FCSTD DOCUMENT  (FreeCAD 1.1R20260325 (Git shallow))
Label: Assembly
License: All rights reserved
LicenseURL: https://en.wikipedia.org/wiki/All_rights_reserved
objects: App::Link×6, App::Point×3, Assembly::JointGroup×3, Assembly::AssemblyObject×3, App::FeaturePython×1
EXTERNAL_REF file=Bracket001.FCStd obj=Body
EXTERNAL_REF file=Bracket001.FCStd obj=Body001
EXTERNAL_REF file=775DC.FCStd obj=Body
EXTERNAL_REF file=nema-17-stepper-motor/17HS4401S stepper motor.FCStd obj=Part
EXTERNAL_REF file=2gt-timing-pulley-2.snapshot.2/Timing Pulley 20 Teeth 2GT Bore 8mm for width 10mm.FCStd obj=Body001
EXTERNAL_REF file=20x20-aluminum-profile-v-slot-1.snapshot.12/20x20 aluminum profile V-slot.FCStd obj=Body

FEATURE [App::Point] Origin001
  Role = Origin
FEATURE [App::Point] Origin003
  Role = Origin
FEATURE [Assembly::JointGroup] Joints001
FEATURE [Assembly::AssemblyObject] Assembly001
  Group = -> [Joints001]
  Origin = -> Origin002
  Type = Assembly
FEATURE [App::Link] Body
  LinkedObject = -> <external Bracket001.FCStd>#Body
FEATURE [App::FeaturePython] GroundedJoint  # Assembly grounded joint (typed FeaturePython)
  ObjectToGround = -> Body
FEATURE [Assembly::JointGroup] Joints
  Group = -> [GroundedJoint]
FEATURE [App::Link] Body001
  LinkPlacement = pos=(0,-4.52995e-06,38) rot=(0,0,1;0rad)
  LinkedObject = -> <external Bracket001.FCStd>#Body001
  Placement = pos=(0,-4.52995e-06,38) rot=(0,0,1;0rad)
FEATURE [App::Link] Body002
  LinkPlacement = pos=(0.341489,0.341488,48.3415) rot=(0,0,1;0rad)
  LinkedObject = -> <external 775DC.FCStd>#Body
  Placement = pos=(0.341489,0.341488,48.3415) rot=(0,0,1;0rad)
FEATURE [App::Link] _17HS4401S_Stepper_Motor  label="17HS4401S Stepper Motor"
  LinkPlacement = pos=(0,4.17233e-06,-35) rot=(0,0,1;0rad)
  LinkedObject = -> <external nema-17-stepper-motor/17HS4401S stepper motor.FCStd>#Part
  Placement = pos=(0,4.17233e-06,-35) rot=(0,0,1;0rad)
FEATURE [App::Link] GT_2_20  label="GT-2-20"
  LinkPlacement = pos=(0,-1.43051e-05,120) rot=(0,0,1;0rad)
  LinkedObject = -> <external 2gt-timing-pulley-2.snapshot.2/Timing Pulley 20 Teeth 2GT Bore 8mm for width 10mm.FCStd>#Body001
  Placement = pos=(0,-1.43051e-05,120) rot=(0,0,1;0rad)
FEATURE [App::Point] Origin005  label="Origin006"
  Role = Origin
FEATURE [Assembly::JointGroup] Joints002
FEATURE [Assembly::AssemblyObject] Assembly002
  Group = -> [Joints002]
  Origin = -> Origin004
  Type = Assembly
FEATURE [App::Link] V_slot_base  label="V-slot base"
  LinkPlacement = pos=(40.612,0.311316,-125.559) rot=(0,0,1;0rad)
  LinkedObject = -> <external 20x20-aluminum-profile-v-slot-1.snapshot.12/20x20 aluminum profile V-slot.FCStd>#Body
  Placement = pos=(40.612,0.311316,-125.559) rot=(0,0,1;0rad)
FEATURE [Assembly::AssemblyObject] Assembly
  Group = -> [Joints,Assembly001,Body,GroundedJoint,Body001,Body002,_17HS4401S_Stepper_Motor,GT_2_20,Assembly002,V_slot_base]
  Origin = -> Origin
  Type = Assembly

RESOLVED EXTERNAL PARTS (link-assembly join: the EXTERNAL_REF files above that resolve inside this repo's crawl, each included once):
---- part 775DC.FCStd = doc fcstd_6108e077a56b ----
FCSTD DOCUMENT  (FreeCAD 1.1R20260325 (Git shallow))
Label: 775DC
License: All rights reserved
LicenseURL: https://en.wikipedia.org/wiki/All_rights_reserved
objects: Sketcher::SketchObject×5, PartDesign::Pad×5, PartDesign::Fillet×4, PartDesign::Body×1, App::Point×1
note: 38 computed .brp shape members not serialized (recipe doc carries the construction recipe); baked Part::Feature solids carry a one-line shape summary decoded from their .brp

FEATURE [Sketcher::SketchObject] Sketch
  ArcFitTolerance = 1e-06
  AttachmentSupport = -> [XY_Plane]
  ExternalTypes = [0]
  FullyConstrained = false
  MakeInternals = false
  MapMode = 5
  _ExternalGeoVersion = 0
  sketch-geometry (1):
    g0: Circle CenterX=-0.540205 CenterY=0 CenterZ=0 NormalX=0 NormalY=0 NormalZ=1 AngleXU=0 Radius=22.5
  constraints (2):
    c: Diameter(g0) = 45
    c: PointOnObject(g0,g-1)
FEATURE [PartDesign::Pad] Pad
  Direction = (0,0,1)
  Length = 66.5
  Length2 = 10
  Profile = -> Sketch
  ReferenceAxis = -> Sketch [N_Axis]
  Refine = true
  SideType = 0
  Suppressed = false
  Type = 0
  Type2 = 0
FEATURE [PartDesign::Fillet] Fillet
  Base = -> Pad [Edge3]
  BaseFeature = -> Pad
  Radius = 3
  Refine = true
  SupportTransform = false
  Suppressed = false
  UseAllEdges = false
FEATURE [Sketcher::SketchObject] Sketch001
  ArcFitTolerance = 1e-06
  AttachmentSupport = -> [Fillet]
  ExternalTypes = [0]
  FullyConstrained = true
  MakeInternals = false
  MapMode = 5
  Placement = pos=(0,0,66.5) rot=(0,0,1;0rad)
  _ExternalGeoVersion = 0
  sketch-geometry (1):
    g0: Circle CenterX=0 CenterY=0 CenterZ=0 NormalX=0 NormalY=0 NormalZ=1 AngleXU=0 Radius=8.75
  constraints (2):
    c: Diameter(g0) = 17.5
    c: Coincident(g0,g-1)
FEATURE [PartDesign::Pad] Pad001
  BaseFeature = -> Fillet
  Direction = (0,0,1)
  Length = 2
  Length2 = 10
  Profile = -> Sketch001
  ReferenceAxis = -> Sketch001 [N_Axis]
  Refine = true
  SideType = 0
  Suppressed = false
  Type = 0
  Type2 = 0
FEATURE [PartDesign::Fillet] Fillet001
  Base = -> Pad001 [Edge8]
  BaseFeature = -> Pad001
  Radius = 1
  Refine = true
  SupportTransform = false
  Suppressed = false
  UseAllEdges = false
FEATURE [Sketcher::SketchObject] Sketch002
  ArcFitTolerance = 1e-06
  AttachmentSupport = -> [Fillet001]
  ExternalTypes = [0]
  FullyConstrained = true
  MakeInternals = false
  MapMode = 5
  Placement = pos=(0,0,68.5) rot=(0,0,1;0rad)
  _ExternalGeoVersion = 0
  sketch-geometry (1):
    g0: Circle CenterX=0 CenterY=0 CenterZ=0 NormalX=0 NormalY=0 NormalZ=1 AngleXU=0 Radius=2.5
  constraints (2):
    c: Diameter(g0) = 5
    c: Coincident(g0,g-1)
FEATURE [PartDesign::Pad] Pad002
  BaseFeature = -> Fillet001
  Direction = (0,0,1)
  Length = 16
  Length2 = 10
  Profile = -> Sketch002
  ReferenceAxis = -> Sketch002 [N_Axis]
  Refine = true
  SideType = 0
  Suppressed = false
  Type = 0
  Type2 = 0
FEATURE [PartDesign::Fillet] Fillet002
  Base = -> Pad002 [Edge11]
  BaseFeature = -> Pad002
  Radius = 1
  Refine = true
  SupportTransform = false
  Suppressed = false
  UseAllEdges = false
FEATURE [Sketcher::SketchObject] Sketch003
  ArcFitTolerance = 1e-06
  AttachmentSupport = -> [Fillet002]
  ExternalTypes = [0]
  FullyConstrained = true
  MakeInternals = false
  MapMode = 5
  Placement = pos=(0,0,0) rot=(1,0,0;3.14159rad)
  _ExternalGeoVersion = 0
  sketch-geometry (1):
    g0: Circle CenterX=0 CenterY=0 CenterZ=0 NormalX=0 NormalY=0 NormalZ=1 AngleXU=0 Radius=8.75
  constraints (2):
    c: Diameter(g0) = 17.5
    c: Coincident(g0,g-1)
FEATURE [PartDesign::Pad] Pad003
  BaseFeature = -> Fillet002
  Direction = (0,0,-1)
  Length = 2
  Length2 = 10
  Profile = -> Sketch003
  ReferenceAxis = -> Sketch003 [N_Axis]
  Refine = true
  SideType = 0
  Suppressed = false
  Type = 0
  Type2 = 0
FEATURE [PartDesign::Fillet] Fillet003
  Base = -> Pad003 [Edge18]
  BaseFeature = -> Pad003
  Radius = 1
  Refine = true
  SupportTransform = false
  Suppressed = false
  UseAllEdges = false
FEATURE [Sketcher::SketchObject] Sketch004
  ArcFitTolerance = 1e-06
  AttachmentSupport = -> [Fillet003]
  ExternalTypes = [0]
  FullyConstrained = true
  MakeInternals = false
  MapMode = 5
  Placement = pos=(0,0,-2) rot=(1,0,0;3.14159rad)
  _ExternalGeoVersion = 0
  sketch-geometry (1):
    g0: Circle CenterX=0 CenterY=0 CenterZ=0 NormalX=0 NormalY=0 NormalZ=1 AngleXU=0 Radius=2.5
  constraints (2):
    c: Diameter(g0) = 5
    c: Coincident(g0,g-1)
FEATURE [PartDesign::Pad] Pad004
  BaseFeature = -> Fillet003
  Direction = (0,0,-1)
  Length = 20
  Length2 = 10
  Profile = -> Sketch004
  ReferenceAxis = -> Sketch004 [N_Axis]
  Refine = true
  SideType = 0
  Suppressed = false
  Type = 0
  Type2 = 0
FEATURE [PartDesign::Body] Body
  AllowCompound = false
  Group = -> [Sketch,Pad,Fillet,Sketch001,Pad001,Fillet001,Sketch002,Pad002,Fillet002,Sketch003,Pad003,Fillet003,Sketch004,Pad004]
  Origin = -> Origin
  Tip = -> Pad004
FEATURE [App::Point] Origin001  label="Origin"
  Role = Origin
---- part Bracket001.FCStd = doc fcstd_f8667adaf7e8 ----
FCSTD DOCUMENT  (FreeCAD 1.1R20260325 (Git shallow))
Label: Bracket001
License: All rights reserved
LicenseURL: https://en.wikipedia.org/wiki/All_rights_reserved
objects: Sketcher::SketchObject×18, PartDesign::Pocket×9, PartDesign::Pad×7, PartDesign::Chamfer×3, PartDesign::Body×2, App::Point×2
note: 95 computed .brp shape members not serialized (recipe doc carries the construction recipe); baked Part::Feature solids carry a one-line shape summary decoded from their .brp

FEATURE [Sketcher::SketchObject] Sketch
  ArcFitTolerance = 1e-06
  AttachmentSupport = -> [XY_Plane]
  ExternalTypes = [0]
  FullyConstrained = true
  MakeInternals = false
  MapMode = 5
  _ExternalGeoVersion = 0
  sketch-geometry (5):
    g0: LineSegment StartX=-31 StartY=-31 StartZ=0 EndX=31 EndY=-31 EndZ=0
    g1: LineSegment StartX=31 StartY=-31 StartZ=0 EndX=31 EndY=31 EndZ=0
    g2: LineSegment StartX=31 StartY=31 StartZ=0 EndX=-31 EndY=31 EndZ=0
    g3: LineSegment StartX=-31 StartY=31 StartZ=0 EndX=-31 EndY=-31 EndZ=0
    g4: GeomPoint [constr] X=0 Y=0 Z=0
  constraints (12):
    c: Coincident(g0,g1)
    c: Coincident(g1,g2)
    c: Coincident(g2,g3)
    c: Coincident(g3,g0)
    c: Horizontal(g0)
    c: Horizontal(g2)
    c: Vertical(g1)
    c: Vertical(g3)
    c: Symmetric(g2,g0,g4)
    c: Distance(g1,g3) = 62
    c: Distance(g0,g2) = 62
    c: Coincident(g4,g-1)
FEATURE [PartDesign::Pad] Pad
  Direction = (0,0,1)
  Length = 8
  Length2 = 10
  Profile = -> Sketch
  ReferenceAxis = -> Sketch [N_Axis]
  Refine = true
  SideType = 0
  Suppressed = false
  Type = 0
  Type2 = 0
FEATURE [Sketcher::SketchObject] Sketch001
  ArcFitTolerance = 1e-06
  AttachmentSupport = -> [Pad]
  ExternalGeometry = -> [Pad]
  ExternalTypes = [0]
  FullyConstrained = true
  MakeInternals = false
  MapMode = 5
  Placement = pos=(0,0,8) rot=(0,0,1;0rad)
  _ExternalGeoVersion = 0
  sketch-geometry (4):
    g0: LineSegment StartX=-31 StartY=31 StartZ=0 EndX=-31 EndY=21 EndZ=0
    g1: LineSegment StartX=-31 StartY=21 StartZ=0 EndX=31 EndY=21 EndZ=0
    g2: LineSegment StartX=31 StartY=21 StartZ=0 EndX=31 EndY=31 EndZ=0
    g3: LineSegment StartX=31 StartY=31 StartZ=0 EndX=-31 EndY=31 EndZ=0
  constraints (11):
    c: Coincident(g0,g1)
    c: Coincident(g1,g2)
    c: Coincident(g2,g3)
    c: Coincident(g3,g0)
    c: Vertical(g0)
    c: Vertical(g2)
    c: Horizontal(g1)
    c: Horizontal(g3)
    c: Distance(g0,g2) = 62
    c: Distance(g1,g3) = 10
    c: Coincident(g0,g-3)
FEATURE [PartDesign::Pad] Pad001
  BaseFeature = -> Pad
  Direction = (0,0,1)
  Length = 30
  Length2 = 10
  Profile = -> Sketch001
  ReferenceAxis = -> Sketch001 [N_Axis]
  Refine = true
  SideType = 0
  Suppressed = false
  Type = 0
  Type2 = 0
FEATURE [Sketcher::SketchObject] Sketch002
  ArcFitTolerance = 1e-06
  AttachmentSupport = -> [Pad001]
  ExternalGeometry = -> [Pad001]
  ExternalTypes = [0]
  FullyConstrained = true
  MakeInternals = false
  MapMode = 5
  Placement = pos=(0,0,8) rot=(0,0,1;0rad)
  _ExternalGeoVersion = 0
  sketch-geometry (4):
    g0: LineSegment StartX=-31 StartY=-31 StartZ=0 EndX=31 EndY=-31 EndZ=0
    g1: LineSegment StartX=31 StartY=-31 StartZ=0 EndX=31 EndY=-21 EndZ=0
    g2: LineSegment StartX=31 StartY=-21 StartZ=0 EndX=-31 EndY=-21 EndZ=0
    g3: LineSegment StartX=-31 StartY=-21 StartZ=0 EndX=-31 EndY=-31 EndZ=0
  constraints (11):
    c: Coincident(g0,g1)
    c: Coincident(g1,g2)
    c: Coincident(g2,g3)
    c: Coincident(g3,g0)
    c: Horizontal(g0)
    c: Horizontal(g2)
    c: Vertical(g1)
    c: Vertical(g3)
    c: Distance(g1,g3) = 62
    c: Distance(g0,g2) = 10
    c: Coincident(g0,g-3)
FEATURE [PartDesign::Pad] Pad002
  BaseFeature = -> Pad001
  Direction = (0,0,1)
  Length = 30
  Length2 = 10
  Profile = -> Sketch002
  ReferenceAxis = -> Sketch002 [N_Axis]
  Refine = true
  SideType = 0
  Suppressed = false
  Type = 0
  Type2 = 0
FEATURE [Sketcher::SketchObject] Sketch003
  ArcFitTolerance = 1e-06
  AttachmentSupport = -> [Pad002]
  ExternalGeometry = -> [Pad002]
  ExternalTypes = [0]
  FullyConstrained = true
  MakeInternals = false
  MapMode = 5
  Placement = pos=(0,0,8) rot=(0,0,1;0rad)
  _ExternalGeoVersion = 0
  sketch-geometry (11):
    g0: LineSegment [constr] StartX=-31 StartY=21 StartZ=0 EndX=-31 EndY=-21 EndZ=0
    g1: LineSegment [constr] StartX=31 StartY=21 StartZ=0 EndX=31 EndY=-21 EndZ=0
    g2: LineSegment [constr] StartX=-15.5 StartY=-15.5 StartZ=0 EndX=15.5 EndY=-15.5 EndZ=0
    g3: LineSegment [constr] StartX=15.5 StartY=-15.5 StartZ=0 EndX=15.5 EndY=15.5 EndZ=0
    g4: LineSegment [constr] StartX=15.5 StartY=15.5 StartZ=0 EndX=-15.5 EndY=15.5 EndZ=0
    g5: LineSegment [constr] StartX=-15.5 StartY=15.5 StartZ=0 EndX=-15.5 EndY=-15.5 EndZ=0
    g6: GeomPoint [constr] X=0 Y=0 Z=0
    g7: Circle CenterX=-15.5 CenterY=15.5 CenterZ=0 NormalX=0 NormalY=0 NormalZ=1 AngleXU=0 Radius=1.6
    g8: Circle CenterX=15.5 CenterY=15.5 CenterZ=0 NormalX=0 NormalY=0 NormalZ=1 AngleXU=0 Radius=1.6
    g9: Circle CenterX=-15.5 CenterY=-15.5 CenterZ=0 NormalX=0 NormalY=0 NormalZ=1 AngleXU=0 Radius=1.6
    g10: Circle CenterX=15.5 CenterY=-15.5 CenterZ=0 NormalX=0 NormalY=0 NormalZ=1 AngleXU=0 Radius=1.6
  constraints (24):
    c: Coincident(g0,g-3)
    c: Coincident(g0,g-4)
    c: Coincident(g1,g-3)
    c: Coincident(g1,g-4)
    c: Coincident(g2,g3)
    c: Coincident(g3,g4)
    c: Coincident(g4,g5)
    c: Coincident(g5,g2)
    c: Horizontal(g2)
    c: Horizontal(g4)
    c: Vertical(g3)
    c: Vertical(g5)
    c: Symmetric(g4,g2,g6)
    c: Distance(g3,g5) = 31
    c: Distance(g2,g4) = 31
    c: Coincident(g6,g-1)
    c: Diameter(g7) = 3.2
    c: Coincident(g7,g4)
    c: Diameter(g8) = 3.2
    c: Coincident(g8,g3)
    c: Diameter(g9) = 3.2
    c: Coincident(g9,g2)
    c: Diameter(g10) = 3.2
    c: Coincident(g10,g2)
FEATURE [PartDesign::Pocket] Pocket
  BaseFeature = -> Pad002
  Direction = (0,0,-1)
  Length = 5
  Length2 = 5
  Profile = -> Sketch003
  ReferenceAxis = -> Sketch003 [N_Axis]
  Refine = true
  SideType = 0
  Suppressed = false
  Type = 1
  Type2 = 0
FEATURE [PartDesign::Chamfer] Chamfer
  Angle = 45
  Base = -> Pocket [Edge31,Edge29,Edge25,Edge27]
  BaseFeature = -> Pocket
  ChamferType = 0
  FlipDirection = false
  Refine = true
  Size = 2
  Size2 = 1
  SupportTransform = false
  Suppressed = false
  UseAllEdges = false
FEATURE [Sketcher::SketchObject] Sketch004
  ArcFitTolerance = 1e-06
  AttachmentSupport = -> [Chamfer]
  ExternalGeometry = -> [Chamfer]
  ExternalTypes = [0]
  FullyConstrained = true
  MakeInternals = false
  MapMode = 5
  Placement = pos=(0,0,38) rot=(0,0,1;0rad)
  _ExternalGeoVersion = 0
  sketch-geometry (5):
    g0: LineSegment [constr] StartX=-21 StartY=31 StartZ=0 EndX=-21 EndY=21 EndZ=0
    g1: LineSegment [constr] StartX=21 StartY=31 StartZ=0 EndX=21 EndY=21 EndZ=0
    g2: LineSegment [constr] StartX=-31 StartY=26 StartZ=0 EndX=31 EndY=26 EndZ=0
    g3: Circle CenterX=-21 CenterY=26 CenterZ=0 NormalX=0 NormalY=0 NormalZ=1 AngleXU=0 Radius=1.75
    g4: Circle CenterX=21 CenterY=26 CenterZ=0 NormalX=0 NormalY=0 NormalZ=1 AngleXU=0 Radius=1.75
  constraints (14):
    c: PointOnObject(g0,g-3)
    c: PointOnObject(g0,g-4)
    c: Vertical(g0)
    c: PointOnObject(g1,g-3)
    c: PointOnObject(g1,g-4)
    c: Vertical(g1)
    c: Distance(g-5,g0) = 10
    c: Distance(g-6,g1) = 10
    c: Symmetric(g-5,g-5,g2)
    c: Symmetric(g-6,g-6,g2)
    c: Diameter(g3) = 3.5
    c: Symmetric(g0,g0,g3)
    c: Diameter(g4) = 3.5
    c: Symmetric(g1,g1,g4)
FEATURE [PartDesign::Pocket] Pocket001
  BaseFeature = -> Chamfer
  Direction = (0,0,-1)
  Length = 12
  Length2 = 5
  Profile = -> Sketch004
  ReferenceAxis = -> Sketch004 [N_Axis]
  Refine = true
  SideType = 0
  Suppressed = false
  Type = 0
  Type2 = 0
FEATURE [Sketcher::SketchObject] Sketch005
  ArcFitTolerance = 1e-06
  AttachmentSupport = -> [Pocket001]
  ExternalGeometry = -> [Pocket001]
  ExternalTypes = [0]
  FullyConstrained = true
  MakeInternals = false
  MapMode = 5
  Placement = pos=(0,0,38) rot=(0,0,1;0rad)
  _ExternalGeoVersion = 0
  sketch-geometry (5):
    g0: LineSegment [constr] StartX=-31 StartY=-26 StartZ=0 EndX=31 EndY=-26 EndZ=0
    g1: LineSegment [constr] StartX=-21 StartY=26 StartZ=0 EndX=-21 EndY=-26 EndZ=0
    g2: LineSegment [constr] StartX=21 StartY=26 StartZ=0 EndX=21 EndY=-26 EndZ=0
    g3: Circle CenterX=-21 CenterY=-26 CenterZ=0 NormalX=0 NormalY=0 NormalZ=1 AngleXU=0 Radius=1.75
    g4: Circle CenterX=21 CenterY=-26 CenterZ=0 NormalX=0 NormalY=0 NormalZ=1 AngleXU=0 Radius=1.75
  constraints (12):
    c: Symmetric(g-5,g-5,g0)
    c: Symmetric(g-6,g-6,g0)
    c: Coincident(g1,g-3)
    c: PointOnObject(g1,g0)
    c: Vertical(g1)
    c: Coincident(g2,g-4)
    c: PointOnObject(g2,g0)
    c: Vertical(g2)
    c: Diameter(g3) = 3.5
    c: Coincident(g3,g1)
    c: Diameter(g4) = 3.5
    c: Coincident(g4,g2)
FEATURE [PartDesign::Pocket] Pocket002
  BaseFeature = -> Pocket001
  Direction = (0,0,-1)
  Length = 12
  Length2 = 5
  Profile = -> Sketch005
  ReferenceAxis = -> Sketch005 [N_Axis]
  Refine = true
  SideType = 0
  Suppressed = false
  Type = 0
  Type2 = 0
FEATURE [Sketcher::SketchObject] Sketch006
  ArcFitTolerance = 1e-06
  AttachmentSupport = -> [Pocket002]
  ExternalTypes = [0]
  FullyConstrained = true
  MakeInternals = false
  MapMode = 5
  Placement = pos=(0,0,8) rot=(0,0,1;0rad)
  _ExternalGeoVersion = 0
  sketch-geometry (1):
    g0: Circle CenterX=0 CenterY=0 CenterZ=0 NormalX=0 NormalY=0 NormalZ=1 AngleXU=0 Radius=12
  constraints (2):
    c: Diameter(g0) = 24
    c: Coincident(g0,g-1)
FEATURE [PartDesign::Pocket] Pocket003
  BaseFeature = -> Pocket002
  Direction = (0,0,-1)
  Length = 5
  Length2 = 5
  Profile = -> Sketch006
  ReferenceAxis = -> Sketch006 [N_Axis]
  Refine = true
  SideType = 0
  Suppressed = false
  Type = 1
  Type2 = 0
FEATURE [Sketcher::SketchObject] Sketch007
  ArcFitTolerance = 1e-06
  AttachmentSupport = -> [XY_Plane001]
  ExternalTypes = [0]
  FullyConstrained = true
  MakeInternals = false
  MapMode = 5
  _ExternalGeoVersion = 0
  sketch-geometry (5):
    g0: LineSegment StartX=-31 StartY=-31 StartZ=0 EndX=31 EndY=-31 EndZ=0
    g1: LineSegment StartX=31 StartY=-31 StartZ=0 EndX=31 EndY=31 EndZ=0
    g2: LineSegment StartX=31 StartY=31 StartZ=0 EndX=-31 EndY=31 EndZ=0
    g3: LineSegment StartX=-31 StartY=31 StartZ=0 EndX=-31 EndY=-31 EndZ=0
    g4: GeomPoint [constr] X=0 Y=0 Z=0
  constraints (12):
    c: Coincident(g0,g1)
    c: Coincident(g1,g2)
    c: Coincident(g2,g3)
    c: Coincident(g3,g0)
    c: Horizontal(g0)
    c: Horizontal(g2)
    c: Vertical(g1)
    c: Vertical(g3)
    c: Symmetric(g2,g0,g4)
    c: Distance(g1,g3) = 62
    c: Distance(g0,g2) = 62
    c: Coincident(g4,g-1)
FEATURE [PartDesign::Pad] Pad003
  Direction = (0,0,1)
  Length = 8
  Length2 = 10
  Profile = -> Sketch007
  ReferenceAxis = -> Sketch007 [N_Axis]
  Refine = true
  SideType = 0
  Suppressed = false
  Type = 0
  Type2 = 0
FEATURE [Sketcher::SketchObject] Sketch008
  ArcFitTolerance = 1e-06
  AttachmentSupport = -> [Pad003]
  ExternalGeometry = -> [Pad003]
  ExternalTypes = [0]
  FullyConstrained = false
  MakeInternals = false
  MapMode = 5
  Placement = pos=(0,0,8) rot=(0,0,1;0rad)
  _ExternalGeoVersion = 0
  sketch-geometry (18):
    g0: LineSegment [constr] StartX=-31 StartY=31 StartZ=0 EndX=-31 EndY=21 EndZ=0
    g1: LineSegment [constr] StartX=-31 StartY=21 StartZ=0 EndX=31 EndY=21 EndZ=0
    g2: LineSegment [constr] StartX=31 StartY=21 StartZ=0 EndX=31 EndY=31 EndZ=0
    g3: LineSegment [constr] StartX=31 StartY=31 StartZ=0 EndX=-31 EndY=31 EndZ=0
    g4: LineSegment [constr] StartX=31 StartY=-31 StartZ=0 EndX=31 EndY=-21 EndZ=0
    g5: LineSegment [constr] StartX=31 StartY=-21 StartZ=0 EndX=-31 EndY=-21 EndZ=0
    g6: LineSegment [constr] StartX=-31 StartY=-21 StartZ=0 EndX=-31 EndY=-31 EndZ=0
    g7: LineSegment [constr] StartX=-31 StartY=-31 StartZ=0 EndX=31 EndY=-31 EndZ=0
    g8: LineSegment [constr] StartX=-31 StartY=-26 StartZ=0 EndX=31 EndY=-26 EndZ=0
    g9: LineSegment [constr] StartX=-31 StartY=26 StartZ=0 EndX=31 EndY=26 EndZ=0
    g10: LineSegment [constr] StartX=-21 StartY=31 StartZ=0 EndX=-21 EndY=21 EndZ=0
    g11: LineSegment [constr] StartX=-21 StartY=21 StartZ=0 EndX=-21 EndY=-26 EndZ=0
    g12: LineSegment [constr] StartX=21 StartY=31 StartZ=0 EndX=21 EndY=21 EndZ=0
    g13: LineSegment [constr] StartX=21 StartY=21 StartZ=0 EndX=21 EndY=-26 EndZ=0
    g14: Circle CenterX=-21 CenterY=26 CenterZ=0 NormalX=0 NormalY=0 NormalZ=1 AngleXU=0 Radius=1.65
    g15: Circle CenterX=21 CenterY=26 CenterZ=0 NormalX=0 NormalY=0 NormalZ=1 AngleXU=0 Radius=1.65
    g16: Circle CenterX=-21 CenterY=-26 CenterZ=0 NormalX=0 NormalY=0 NormalZ=1 AngleXU=0 Radius=1.65
    g17: Circle CenterX=20.8764 CenterY=-26 CenterZ=0 NormalX=0 NormalY=0 NormalZ=1 AngleXU=0 Radius=1.65
  constraints (48):
    c: Coincident(g0,g1)
    c: Coincident(g1,g2)
    c: Coincident(g2,g3)
    c: Coincident(g3,g0)
    c: Vertical(g0)
    c: Vertical(g2)
    c: Horizontal(g1)
    c: Horizontal(g3)
    c: Distance(g0,g2) = 62
    c: Distance(g1,g3) = 10
    c: Coincident(g0,g-3)
    c: Coincident(g4,g5)
    c: Coincident(g5,g6)
    c: Coincident(g6,g7)
    c: Coincident(g7,g4)
    c: Vertical(g4)
    c: Vertical(g6)
    c: Horizontal(g5)
    c: Horizontal(g7)
    c: Distance(g4,g6) = 62
    c: Distance(g5,g7) = 10
    c: Coincident(g4,g-4)
    c: Symmetric(g6,g6,g8)
    c: Symmetric(g4,g4,g8)
    c: Symmetric(g0,g0,g9)
    c: Symmetric(g2,g2,g9)
    c: PointOnObject(g10,g3)
    c: PointOnObject(g10,g1)
    c: Vertical(g10)
    c: Distance(g0,g10) = 10
    c: Coincident(g11,g10)
    c: PointOnObject(g11,g8)
    c: Vertical(g11)
    c: PointOnObject(g12,g3)
    c: PointOnObject(g12,g1)
    c: Vertical(g12)
    c: Distance(g2,g12) = 10
    c: Coincident(g13,g12)
    c: PointOnObject(g13,g8)
    c: Vertical(g13)
    c: Diameter(g14) = 3.3
    c: Symmetric(g10,g10,g14)
    c: Diameter(g15) = 3.3
    c: Symmetric(g12,g12,g15)
    c: Diameter(g16) = 3.3
    c: Coincident(g16,g11)
    c: Diameter(g17) = 3.3
    c: PointOnObject(g17,g8)
FEATURE [PartDesign::Pocket] Pocket004
  BaseFeature = -> Pad003
  Direction = (0,0,-1)
  Length = 5
  Length2 = 5
  Profile = -> Sketch008
  ReferenceAxis = -> Sketch008 [N_Axis]
  Refine = true
  SideType = 0
  Suppressed = false
  Type = 1
  Type2 = 0
FEATURE [PartDesign::Chamfer] Chamfer001
  Angle = 45
  Base = -> Pocket004 [Edge18,Edge20,Edge19,Edge17]
  BaseFeature = -> Pocket004
  ChamferType = 0
  FlipDirection = false
  Refine = true
  Size = 2
  Size2 = 1
  SupportTransform = false
  Suppressed = false
  UseAllEdges = false
FEATURE [Sketcher::SketchObject] Sketch009
  ArcFitTolerance = 1e-06
  AttachmentSupport = -> [Chamfer001]
  ExternalTypes = [0]
  FullyConstrained = true
  MakeInternals = false
  MapMode = 5
  Placement = pos=(0,0,8) rot=(0,0,1;0rad)
  _ExternalGeoVersion = 0
  sketch-geometry (2):
    g0: Circle CenterX=0 CenterY=0 CenterZ=0 NormalX=0 NormalY=0 NormalZ=1 AngleXU=0 Radius=21.25
    g1: Circle CenterX=0 CenterY=0 CenterZ=0 NormalX=0 NormalY=0 NormalZ=1 AngleXU=0 Radius=27.75
  constraints (4):
    c: Diameter(g0) = 42.5
    c: Coincident(g0,g-1)
    c: Diameter(g1) = 55.5
    c: Coincident(g1,g0)
FEATURE [PartDesign::Pad] Pad004
  BaseFeature = -> Chamfer001
  Direction = (0,0,1)
  Length = 34
  Length2 = 10
  Profile = -> Sketch009
  ReferenceAxis = -> Sketch009 [N_Axis]
  Refine = true
  SideType = 0
  Suppressed = false
  Type = 0
  Type2 = 0
FEATURE [Sketcher::SketchObject] Sketch010
  ArcFitTolerance = 1e-06
  AttachmentSupport = -> [Pad004]
  ExternalTypes = [0]
  FullyConstrained = true
  MakeInternals = false
  MapMode = 5
  Placement = pos=(0,0,8) rot=(0,0,1;0rad)
  _ExternalGeoVersion = 0
  sketch-geometry (1):
    g0: Circle CenterX=0 CenterY=0 CenterZ=0 NormalX=0 NormalY=0 NormalZ=1 AngleXU=0 Radius=12
  constraints (2):
    c: Diameter(g0) = 24
    c: Coincident(g0,g-1)
FEATURE [PartDesign::Pocket] Pocket005
  BaseFeature = -> Pad004
  Direction = (0,0,-1)
  Length = 5
  Length2 = 5
  Profile = -> Sketch010
  ReferenceAxis = -> Sketch010 [N_Axis]
  Refine = true
  SideType = 0
  Suppressed = false
  Type = 1
  Type2 = 0
FEATURE [Sketcher::SketchObject] Sketch011
  ArcFitTolerance = 1e-06
  AttachmentSupport = -> [Pocket005]
  ExternalTypes = [0]
  FullyConstrained = false
  MakeInternals = false
  MapMode = 5
  Placement = pos=(0,0,42) rot=(0,0,1;0rad)
  _ExternalGeoVersion = 0
  sketch-geometry (5):
    g0: LineSegment StartX=-2.38976 StartY=32.2002 StartZ=0 EndX=-2.38976 EndY=16.9452 EndZ=0
    g1: LineSegment StartX=-2.38976 StartY=16.9452 StartZ=0 EndX=2.38975 EndY=16.9452 EndZ=0
    g2: LineSegment StartX=2.38975 StartY=16.9452 StartZ=0 EndX=2.38975 EndY=32.2002 EndZ=0
    g3: LineSegment StartX=2.38975 StartY=32.2002 StartZ=0 EndX=-2.38976 EndY=32.2002 EndZ=0
    g4: GeomPoint [constr] X=0 Y=24.5727 Z=0
  constraints (10):
    c: Coincident(g0,g1)
    c: Coincident(g1,g2)
    c: Coincident(g2,g3)
    c: Coincident(g3,g0)
    c: Vertical(g0)
    c: Vertical(g2)
    c: Horizontal(g1)
    c: Horizontal(g3)
    c: Symmetric(g2,g0,g4)
    c: PointOnObject(g4,g-2)
FEATURE [PartDesign::Pocket] Pocket006
  BaseFeature = -> Pocket005
  Direction = (0,0,-1)
  Length = 34
  Length2 = 5
  Profile = -> Sketch011
  ReferenceAxis = -> Sketch011 [N_Axis]
  Refine = true
  SideType = 0
  Suppressed = false
  Type = 0
  Type2 = 0
FEATURE [Sketcher::SketchObject] Sketch012
  ArcFitTolerance = 1e-06
  AttachmentSupport = -> [Pocket006]
  ExternalTypes = [0]
  FullyConstrained = false
  MakeInternals = false
  MapMode = 5
  Placement = pos=(0,0,8) rot=(0,0,1;0rad)
  _ExternalGeoVersion = 0
  sketch-geometry (2):
    g0: Circle CenterX=-18.7387 CenterY=0 CenterZ=0 NormalX=0 NormalY=0 NormalZ=1 AngleXU=0 Radius=2.4
    g1: Circle CenterX=18.7387 CenterY=0 CenterZ=0 NormalX=0 NormalY=0 NormalZ=1 AngleXU=0 Radius=2.4
  constraints (3):
    c: Diameter(g0) = 4.8
    c: PointOnObject(g0,g-1)
    c: Diameter(g1) = 4.8
FEATURE [PartDesign::Pocket] Pocket007
  BaseFeature = -> Pocket006
  Direction = (0,0,-1)
  Length = 5
  Length2 = 5
  Profile = -> Sketch012
  ReferenceAxis = -> Sketch012 [N_Axis]
  Refine = true
  SideType = 0
  Suppressed = false
  Type = 1
  Type2 = 0
FEATURE [Sketcher::SketchObject] Sketch013
  ArcFitTolerance = 1e-06
  AttachmentSupport = -> [Pocket007]
  ExternalTypes = [0]
  FullyConstrained = true
  MakeInternals = false
  MapMode = 5
  Placement = pos=(0,0,8) rot=(0,0,1;0rad)
  _ExternalGeoVersion = 0
FEATURE [PartDesign::Body] Body001
  AllowCompound = false
  Group = -> [Sketch007,Pad003,Sketch008,Pocket004,Chamfer001,Sketch009,Pad004,Sketch010,Pocket005,Sketch011,Pocket006,Sketch012,Pocket007,Sketch013]
  Origin = -> Origin001
  Placement = pos=(0,0,38) rot=(0,0,1;0rad)
  Tip = -> Pocket007
FEATURE [App::Point] Origin002  label="Origin"
  Role = Origin
FEATURE [App::Point] Origin003  label="Origin"
  Role = Origin
FEATURE [Sketcher::SketchObject] Sketch014
  ArcFitTolerance = 1e-06
  AttachmentSupport = -> [Pocket003]
  ExternalGeometry = -> [Pocket003]
  ExternalTypes = [0,0]
  FullyConstrained = false
  MakeInternals = false
  MapMode = 5
  Placement = pos=(0,0,38) rot=(0,0,1;0rad)
  _ExternalGeoVersion = 1
  sketch-geometry (18):
    g0: LineSegment [constr] StartX=-21 StartY=27.75 StartZ=0 EndX=-21 EndY=24.25 EndZ=0
    g1: LineSegment [constr] StartX=-22.75 StartY=26 StartZ=0 EndX=-19.25 EndY=26 EndZ=0
    g2: Circle CenterX=-21 CenterY=27.75 CenterZ=0 NormalX=0 NormalY=0 NormalZ=1 AngleXU=0 Radius=0.3
    g3: Circle CenterX=-19.25 CenterY=26 CenterZ=0 NormalX=0 NormalY=0 NormalZ=1 AngleXU=0 Radius=0.3
    g4: Circle CenterX=-21 CenterY=24.25 CenterZ=0 NormalX=0 NormalY=0 NormalZ=1 AngleXU=0 Radius=0.3
    g5: Circle CenterX=-22.75 CenterY=26 CenterZ=0 NormalX=0 NormalY=0 NormalZ=1 AngleXU=0 Radius=0.3
    g6: Circle CenterX=19.25 CenterY=26 CenterZ=0 NormalX=0 NormalY=0 NormalZ=1 AngleXU=0 Radius=0.3
    g7: Circle CenterX=21 CenterY=27.75 CenterZ=0 NormalX=0 NormalY=0 NormalZ=1 AngleXU=0 Radius=0.3
    g8: Circle CenterX=22.75 CenterY=26 CenterZ=0 NormalX=0 NormalY=0 NormalZ=1 AngleXU=0 Radius=0.3
    g9: Circle CenterX=21 CenterY=24.25 CenterZ=0 NormalX=0 NormalY=0 NormalZ=1 AngleXU=0 Radius=0.3
    g10: Circle CenterX=22.75 CenterY=-26 CenterZ=0 NormalX=0 NormalY=0 NormalZ=1 AngleXU=0 Radius=0.3
    g11: Circle CenterX=21 CenterY=-27.75 CenterZ=0 NormalX=0 NormalY=0 NormalZ=1 AngleXU=0 Radius=0.3
    g12: Circle CenterX=21 CenterY=-24.25 CenterZ=0 NormalX=0 NormalY=0 NormalZ=1 AngleXU=0 Radius=0.3
    g13: Circle CenterX=19.25 CenterY=-26 CenterZ=0 NormalX=0 NormalY=0 NormalZ=1 AngleXU=0 Radius=0.3
    g14: Circle CenterX=-19.25 CenterY=-26 CenterZ=0 NormalX=0 NormalY=0 NormalZ=1 AngleXU=0 Radius=0.3
    g15: Circle CenterX=-21 CenterY=-27.75 CenterZ=0 NormalX=0 NormalY=0 NormalZ=1 AngleXU=0 Radius=0.3
    g16: Circle CenterX=-22.75 CenterY=-26 CenterZ=0 NormalX=0 NormalY=0 NormalZ=1 AngleXU=0 Radius=0.3
    g17: Circle CenterX=-21 CenterY=-24.25 CenterZ=0 NormalX=0 NormalY=0 NormalZ=1 AngleXU=0 Radius=0.3
  constraints (28):
    c: PointOnObject(g0,g-3)
    c: PointOnObject(g-3,g0)
    c: Vertical(g0)
    c: PointOnObject(g1,g-3)
    c: PointOnObject(g1,g-3)
    c: Horizontal(g1)
    c: PointOnObject(g-3,g1)
    c: Diameter(g2) = 0.6
    c: Coincident(g2,g0)
    c: Diameter(g3) = 0.6
    c: Coincident(g3,g1)
    c: PointOnObject(g0,g-3)
    c: Diameter(g4) = 0.6
    c: Coincident(g4,g0)
    c: Diameter(g5) = 0.6
    c: Coincident(g5,g1)
    c: Diameter(g7) = 0.6
    c: Diameter(g6) = 0.6
    c: Diameter(g9) = 0.6
    c: Diameter(g8) = 0.6
    c: Diameter(g15) = 0.6
    c: Diameter(g14) = 0.6
    c: Diameter(g17) = 0.6
    c: Diameter(g16) = 0.6
    c: Diameter(g11) = 0.6
    c: Diameter(g13) = 0.6
    c: Diameter(g12) = 0.6
    c: Diameter(g10) = 0.6
FEATURE [PartDesign::Pad] Pad005
  BaseFeature = -> Pocket003
  Direction = (0,0,1)
  Length = 14
  Length2 = 10
  Profile = -> Sketch014
  ReferenceAxis = -> Sketch014 [N_Axis]
  Refine = true
  Reversed = true
  SideType = 0
  Suppressed = false
  Type = 0
  Type2 = 0
FEATURE [Sketcher::SketchObject] Sketch015
  ArcFitTolerance = 1e-06
  AttachmentSupport = -> [Pad005]
  ExternalGeometry = -> [Sketch005]
  ExternalTypes = [0,0]
  FullyConstrained = true
  MakeInternals = false
  MapMode = 5
  Placement = pos=(0,0,38) rot=(0,0,1;0rad)
  _ExternalGeoVersion = 1
FEATURE [Sketcher::SketchObject] Sketch016
  ArcFitTolerance = 1e-06
  AttachmentSupport = -> [Pad005]
  ExternalGeometry = -> [Pad005]
  ExternalTypes = [0,0]
  FullyConstrained = true
  MakeInternals = false
  MapMode = 5
  Placement = pos=(0,0,8) rot=(0,0,1;0rad)
  _ExternalGeoVersion = 1
  sketch-geometry (4):
    g0: LineSegment StartX=31 StartY=21 StartZ=0 EndX=21 EndY=21 EndZ=0
    g1: LineSegment StartX=21 StartY=21 StartZ=0 EndX=21 EndY=-21 EndZ=0
    g2: LineSegment StartX=21 StartY=-21 StartZ=0 EndX=31 EndY=-21 EndZ=0
    g3: LineSegment StartX=31 StartY=-21 StartZ=0 EndX=31 EndY=21 EndZ=0
  constraints (11):
    c: Coincident(g0,g1)
    c: Coincident(g1,g2)
    c: Coincident(g2,g3)
    c: Coincident(g3,g0)
    c: Horizontal(g0)
    c: Horizontal(g2)
    c: Vertical(g1)
    c: Vertical(g3)
    c: Distance(g1,g3) = 10
    c: Coincident(g0,g-3)
    c: PointOnObject(g1,g-4)
FEATURE [PartDesign::Pad] Pad006
  BaseFeature = -> Pad005
  Direction = (0,0,1)
  Length = 30
  Length2 = 10
  Profile = -> Sketch016
  ReferenceAxis = -> Sketch016 [N_Axis]
  Refine = true
  SideType = 0
  Suppressed = false
  Type = 0
  Type2 = 0
FEATURE [Sketcher::SketchObject] Sketch017
  ArcFitTolerance = 1e-06
  AttachmentSupport = -> [Pad006]
  ExternalGeometry = -> [Pad006]
  ExternalTypes = [0,0]
  FullyConstrained = true
  MakeInternals = false
  MapMode = 5
  Placement = pos=(21,0,0) rot=(0.57735,-0.57735,-0.57735;2.0944rad)
  _ExternalGeoVersion = 1
  sketch-geometry (3):
    g0: LineSegment [constr] StartX=-21 StartY=23 StartZ=0 EndX=21 EndY=23 EndZ=0
    g1: Circle CenterX=-11 CenterY=23 CenterZ=0 NormalX=0 NormalY=0 NormalZ=1 AngleXU=0 Radius=2.1
    g2: Circle CenterX=13 CenterY=23 CenterZ=0 NormalX=0 NormalY=0 NormalZ=1 AngleXU=0 Radius=2.1
  constraints (8):
    c: Symmetric(g-3,g-3,g0)
    c: Symmetric(g-4,g-4,g0)
    c: Diameter(g1) = 4.2
    c: PointOnObject(g1,g0)
    c: Diameter(g2) = 4.2
    c: PointOnObject(g2,g0)
    c: DistanceX(g1,g2) = 24
    c: Distance(g1,g-3) = 10
FEATURE [PartDesign::Pocket] Pocket008
  BaseFeature = -> Pad006
  Direction = (1,0,0)
  Length = 5
  Length2 = 5
  Profile = -> Sketch017
  ReferenceAxis = -> Sketch017 [N_Axis]
  Refine = true
  SideType = 0
  Suppressed = false
  Type = 1
  Type2 = 0
FEATURE [PartDesign::Chamfer] Chamfer002
  Angle = 45
  Base = -> Pocket008 [Edge47,Edge46]
  BaseFeature = -> Pocket008
  ChamferType = 0
  FlipDirection = false
  Refine = true
  Size = 2
  Size2 = 1
  SupportTransform = false
  Suppressed = false
  UseAllEdges = false
FEATURE [PartDesign::Body] Body
  AllowCompound = false
  Group = -> [Sketch,Pad,Sketch001,Pad001,Sketch002,Pad002,Sketch003,Pocket,Chamfer,Sketch004,Pocket001,Sketch005,Pocket002,Sketch006,Pocket003,Sketch014,Pad005,Sketch015,Sketch016,Pad006,Sketch017,Pocket008,Chamfer002]
  Origin = -> Origin
  Tip = -> Chamfer002
